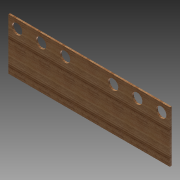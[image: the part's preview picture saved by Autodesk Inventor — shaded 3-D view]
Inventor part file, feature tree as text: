
AUTODESK INVENTOR PART (.ipt)
format: ipt  version: 2012 (Build 160160000, 160)  size: 103,424 bytes
history: native  units: in
note: dims shown in document units (in); Inventor stores cm internally (conversion verified against a paired STEP export)
features: extrude x1, sketch x1
ambient origin geometry x8: Origin, YZ Plane, XZ Plane, XY Plane, X Axis, Y Axis, Z Axis, Center Point
bodies: Solid1 (feature_tree)
feature tree (2):
  extrude  "Extrusion1"  Depth=23.5in
  sketch  "Sketch1"  dims[d0=7.5in d1=23.5in d11=0.25in d12=0.0in d13=1.5in d14=1.5in d15=7.0in d16=7.0in d17=3.5in d18=3.5in d19=1.25in d20=23.5in d21=1.25in d22=1.25in d23=1.25in]
